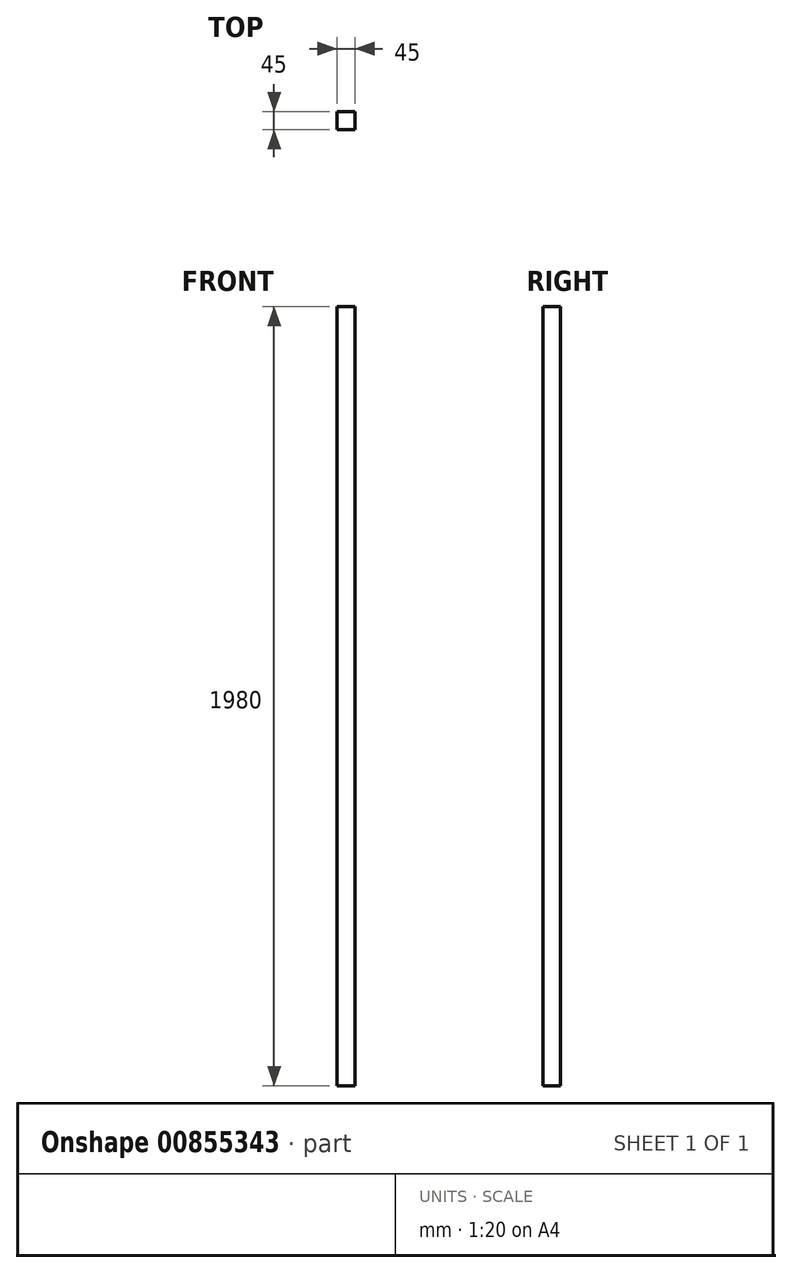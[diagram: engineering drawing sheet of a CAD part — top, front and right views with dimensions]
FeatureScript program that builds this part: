
annotation { "Feature Type Name" : "Feature", "Feature Type Description" : "" }
export const myFeature = defineFeature(function(context is Context, id is Id, definition is map)
    precondition{}
    {
        {
            var Q0;
            Q0=qCreatedBy(makeId("Top.planeOp"),FACE);
            var sketch = newSketch(context, id + "F0", { "sketchPlane" : qUnion([Q0])});
            skLineSegment(sketch, "E0.bottom", {"start": v(0, 0) * mm, "end": v(45, 0) * mm});
            skLineSegment(sketch, "E0.top", {"start": v(0, 45) * mm, "end": v(45, 45) * mm});
            skLineSegment(sketch, "E0.left", {"start": v(0, 0) * mm, "end": v(0, 45) * mm});
            skLineSegment(sketch, "E0.right", {"start": v(45, 0) * mm, "end": v(45, 45) * mm});
            skSolve(sketch);
        }
        {
            var Q0;
            Q0 = qSketchRegion(id + "F0", true);
            extrude(context, id + "F1", {"entities" : qUnion([Q0]), "depth" : 1980 * mm, "offsetDistance" : 25 * mm});
        }
    });
